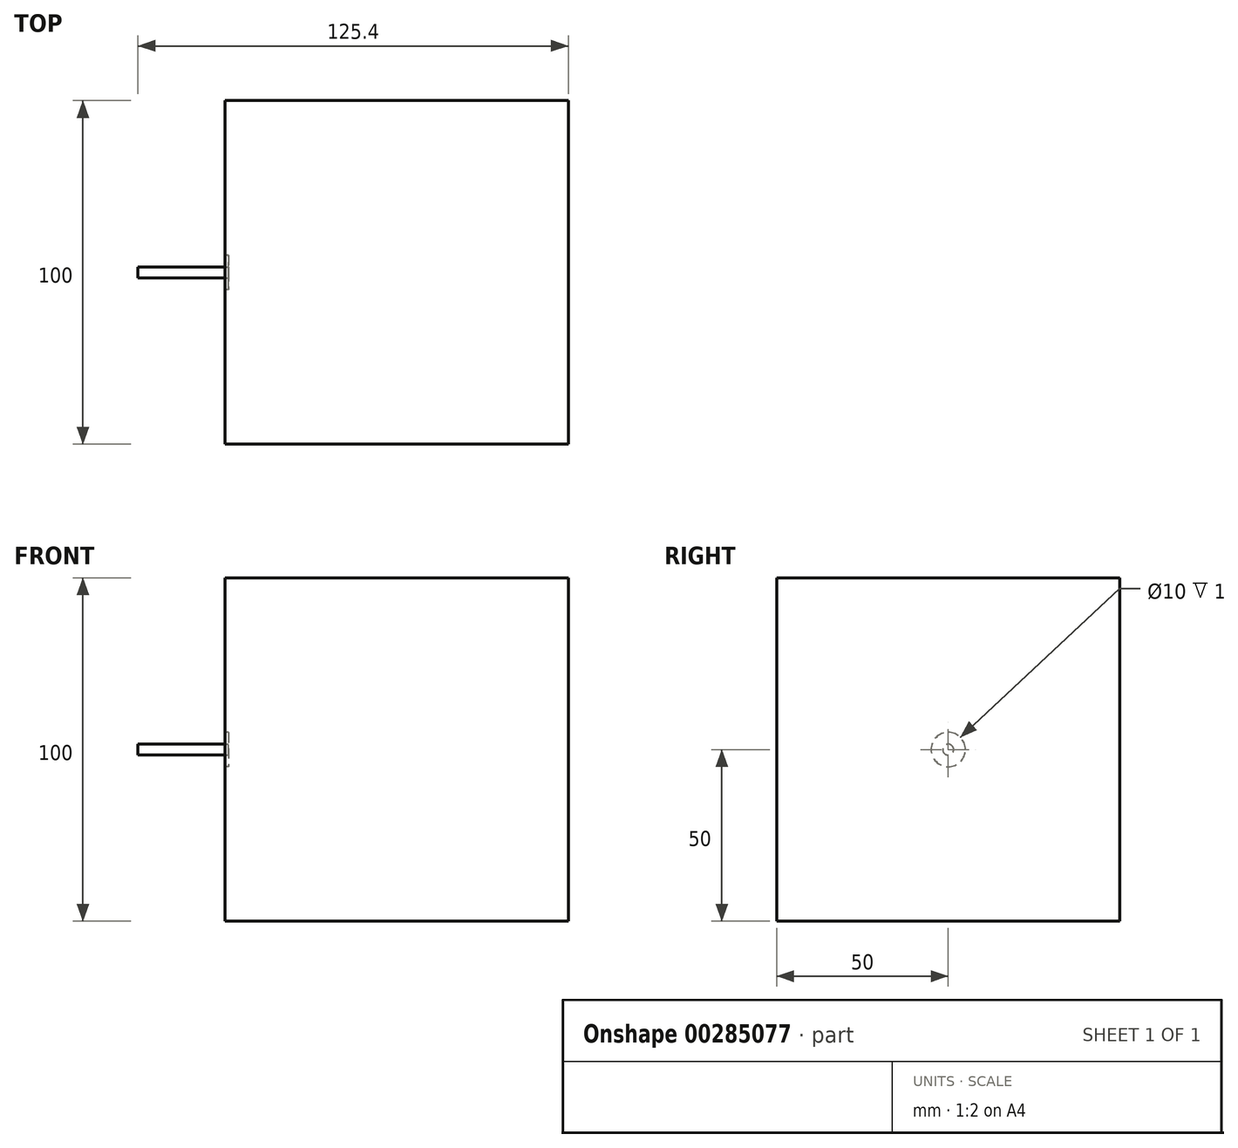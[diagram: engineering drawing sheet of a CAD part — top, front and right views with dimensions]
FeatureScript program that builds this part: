
annotation { "Feature Type Name" : "Feature", "Feature Type Description" : "" }
export const myFeature = defineFeature(function(context is Context, id is Id, definition is map)
    precondition{}
    {
        {
            var Q0;
            Q0=qCreatedBy(makeId("Right.planeOp"),FACE);
            var sketch = newSketch(context, id + "F0", { "sketchPlane" : qUnion([Q0])});
            skCircle(sketch, "E0", {"center": v(0, 0) * mm, "radius": 1.59 * mm});
            skSolve(sketch);
        }
        {
            var Q0;
            Q0 = qSketchRegion(id + "F0", true);
            extrude(context, id + "F1", {"entities" : qUnion([Q0]), "oppositeDirection" : true, "depth" : 25.4 * mm});
        }
        {
            var Q0;
            Q0=qCreatedBy(makeId("Right.planeOp"),FACE);
            var sketch = newSketch(context, id + "F2", { "sketchPlane" : qUnion([Q0])});
            skLineSegment(sketch, "E1.bottom", {"start": v(50, -50) * mm, "end": v(-50, -50) * mm});
            skLineSegment(sketch, "E1.top", {"start": v(50, 50) * mm, "end": v(-50, 50) * mm});
            skLineSegment(sketch, "E1.left", {"start": v(50, -50) * mm, "end": v(50, 50) * mm});
            skLineSegment(sketch, "E1.right", {"start": v(-50, -50) * mm, "end": v(-50, 50) * mm});
            skPoint(sketch, "E1.middle", {"position": v(0, 0) * mm});
            skSolve(sketch);
        }
        {
            var Q0;
            Q0 = qSketchRegion(id + "F2", true);
            extrude(context, id + "F3", {"entities" : qUnion([Q0]), "operationType" : NewBodyOperationType.ADD, "depth" : 100 * mm});
        }
        {
            var Q0;
            Q0=makeQuery(id+"F3.opExtrude","CAP_FACE",FACE,{"disambiguationData":[OSD([sQuery(id+"F2.wireOp",EDGE,"E1.bottom"),sQuery(id+"F2.wireOp",EDGE,"E1.top"),sQuery(id+"F2.wireOp",EDGE,"E1.left"),sQuery(id+"F2.wireOp",EDGE,"E1.right")])],"isStart":true});
            var sketch = newSketch(context, id + "F4", { "sketchPlane" : qUnion([Q0])});
            skCircle(sketch, "E2.0", {"center": v(0, 0) * mm, "radius": 1.59 * mm});
            skCircle(sketch, "E3", {"center": v(0, 0) * mm, "radius": 5 * mm});
            skSolve(sketch);
        }
        {
            var Q0;
            Q0=makeQuery(id+"F4.imprint","IMPRINT",FACE,{"disambiguationData":[TD([[makeQuery(id+"F4.imprint","IMPRINT",EDGE,{"derivedFrom":sQuery(id+"F4.wireOp",EDGE,"E2.0")}),1.0]])]});
            extrude(context, id + "F5", {"entities" : qUnion([Q0]), "operationType" : NewBodyOperationType.REMOVE, "oppositeDirection" : true, "depth" : 1 * mm});
        }
    });
